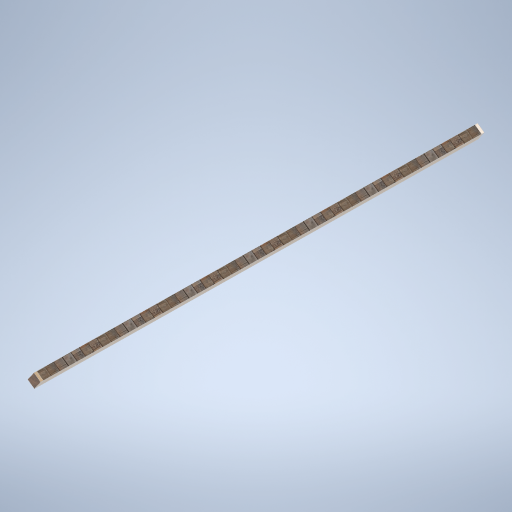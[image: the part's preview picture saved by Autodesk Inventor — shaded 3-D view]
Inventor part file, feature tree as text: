
AUTODESK INVENTOR PART (.ipt)
format: ipt  version: 2024.2 (Build 282272000, 272)  size: 302,592 bytes
history: native  units: in
note: dims shown in document units (in); Inventor stores cm internally (conversion verified against a paired STEP export)
features: sketch x5, other x3, plane x2
ambient origin geometry x8: Origin, YZ Plane, XZ Plane, XY Plane, X Axis, Y Axis, Z Axis, Center Point
bodies: Solid1 (feature_tree)
feature tree (10):
  other  "support_beam_segment_0106_MIR.ipt"
  other  "Solid1::support_beam_segment_0106_MIR.ipt"
  other  "TaggingFeature1"
  sketch  "Sketch1"  dims[d0=0.3937in]
  sketch  "Sketch2"
  sketch  "Sketch3"
  sketch  "Sketch4"
  sketch  "Sketch5"
  plane  "Work Plane1"
  plane  "Work Plane2"
